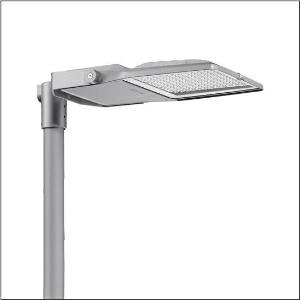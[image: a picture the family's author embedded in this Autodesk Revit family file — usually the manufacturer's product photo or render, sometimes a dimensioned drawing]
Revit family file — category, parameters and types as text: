
# Revit family: floodlight_fl_21_iq_midi___pl43_5xa7781e2a3a_1390
name_source: partatom
category: Lighting Fixtures
units: mm (PartAtom-declared; Revit-internal decimal feet)

## family parameters
Cut with Voids When Loaded = No
Host = Face
Light Source = No
Part Type = Normal
Room Calculation Point = No
Round Connector Dimension = Use Diameter
Shared = No

## types (1)
- --- (1 x LED, 27540 lm, 208.1 W, 3000K)
    Apparent Load = 208 VA
    CIE Flux Codes = 27 78 99 100 100
    Color Rendering = 70
    Color Temperature = 3000K
    Default Elevation = 1800 mm
    Description = Floodlight FL 21 iQ midi, floodlight, primary light control with lens, of PMMA, primary optical cover: protective disc, of toughened safety glass, transparent, light distribution: PL43, light emission: direct distribution, installation type: surface-mounted, LED, High Power LED, rated luminous flux: 27.540lm, luminous efficacy: 132lm/W, light colour: 730, colour temperature: 3000K, control gear: ECG iQ, control: optimised constant luminous flux control (CLO 2.0), Desk-Remote (wireless, voltage-free reading and setting of iQ features in the workshop via application-optimized NFC function/RFID function), Light-Fading, Smart-Wire, Night-Set, Lumen-Switch, Temp-Guard, Auto-Match, with terminal, 6-pole, mains connection: 220..240V, AC, 50/60Hz, start of lifetime: 208W, end of service life: 227W, reduction: 90W, luminaire housing, of diecast aluminium, powder-coated, Siteco® metallic grey (DB 702S), corrosivity category C5 mid according to DIN EN ISO 12944, sealing non-destructively replaceable, please order mast flange separately, mast bracket, of steel, galvanised, powder-coated, Siteco® metallic grey (DB 702S), protection rating (complete): IP66, insulation class (complete): insulation class II (safety insulation), certification: CE, protection symbol: D, impact resistance: IK08, permissible operating ambient temperature: -40..+40°C, permissible operating ambient temperature for outdoor applications: -40..+50°C, standard: DIN EN 12944, LABS conformity tested according to VDMA 24364:2018-05, packaging unit: 1 piece

Light Distribution: PL43
    Height = 76 mm
    Lamp = 1 x LED
    Lamp Light Flux = 27540 lm
    Lamp Power = 208.1 W
    Lamp count = 1
    Length = 657 mm
    Luminous efficacy = 132 lm/W
    Manufacturer = Siteco
    ModVariant = No
    Model = 5XA7781E2A3A
    Number of Poles = 1
    OnlyDefault = Yes
    Power Factor = 1
    Product Name = Floodlight FL 21 iQ midi | PL43
    Product group = floodlight | pylon annexe
    ProductGroupID = 6200
    Protection Class = Protection class II
    Protection Degree = IP 66
    RLX_Detail_Level = 1
    RLX_Emergency_Light_Flux = 0 lm
    RLX_Emergency_Type = 0
    RLX_Emergency_Type_DB = No
    RlxData = <blob elided: 153597 chars, md5=5daeb74b>
    Socket = socket
    Standby Power = 0 W
    System Light Flux = 27540 lm
    System Power = 208 W
    Type Comments = factory setting: luminous flux: 100 % | dim-lin: 254 | 710 mA
    Type Image = l_1007123.jpg
    URL = http://relux.com
    VarID = @adj_053661
    Voltage = 0 V
    Weight = 0.00 kg
    Width = 442 mm

## geometry (parser evidence)
native form markers: Blend x4, Sweep x13
no freeform markers — native parametric forms only
